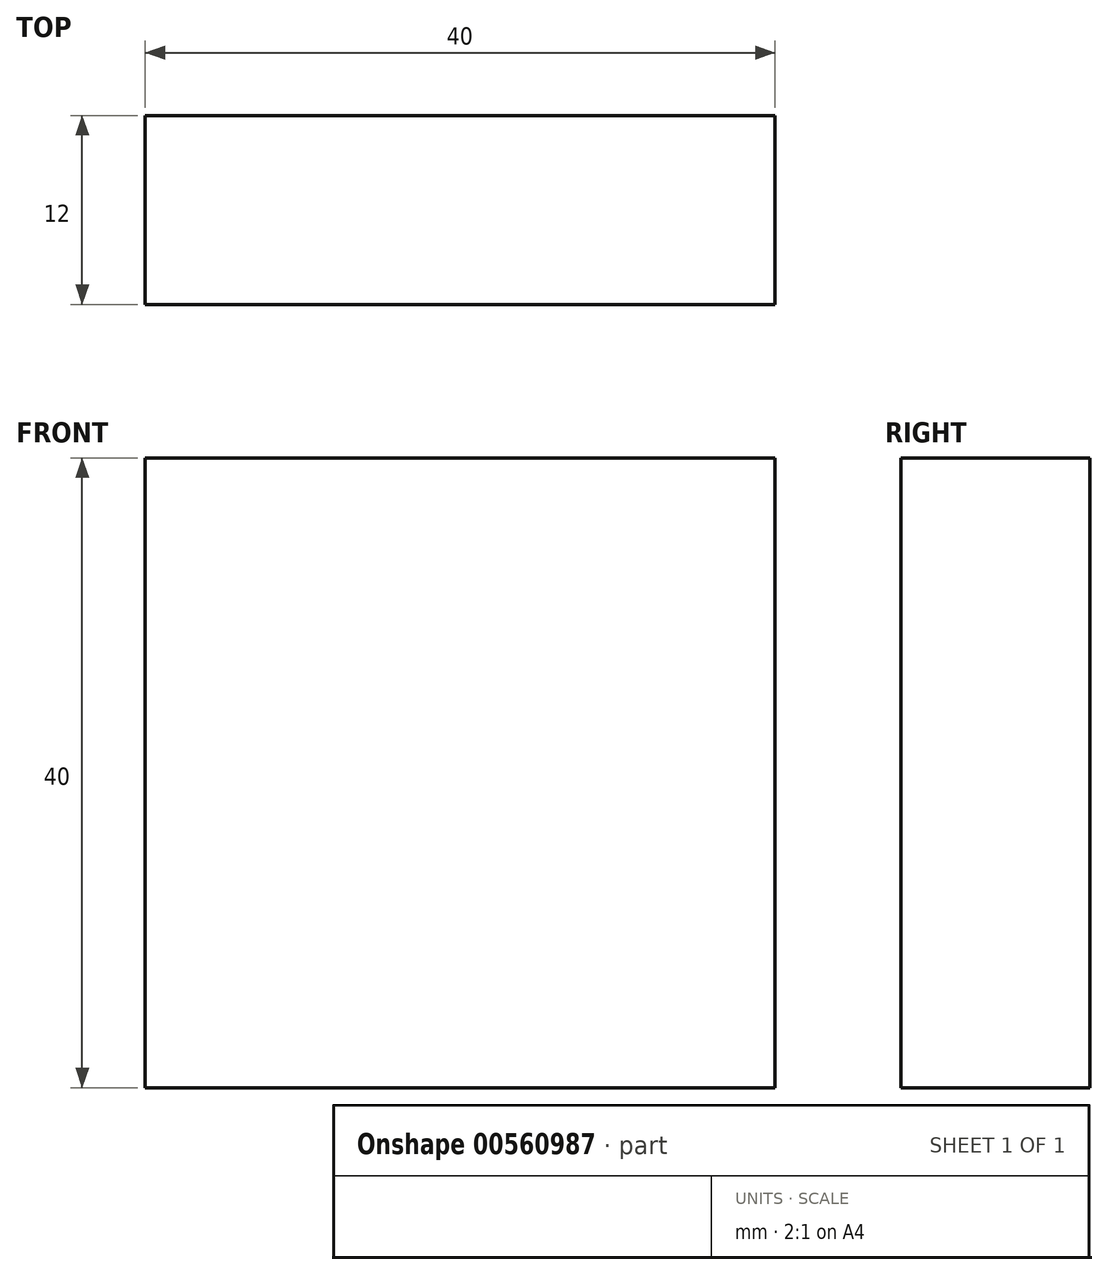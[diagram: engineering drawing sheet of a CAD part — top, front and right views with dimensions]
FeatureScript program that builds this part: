
annotation { "Feature Type Name" : "Feature", "Feature Type Description" : "" }
export const myFeature = defineFeature(function(context is Context, id is Id, definition is map)
    precondition{}
    {
        {
            var Q0;
            Q0=qCreatedBy(makeId("Front.planeOp"),FACE);
            var sketch = newSketch(context, id + "F0", { "sketchPlane" : qUnion([Q0])});
            skLineSegment(sketch, "E0.bottom", {"start": v(20, -20) * mm, "end": v(-20, -20) * mm});
            skLineSegment(sketch, "E0.top", {"start": v(20, 20) * mm, "end": v(-20, 20) * mm});
            skLineSegment(sketch, "E0.left", {"start": v(20, -20) * mm, "end": v(20, 20) * mm});
            skLineSegment(sketch, "E0.right", {"start": v(-20, -20) * mm, "end": v(-20, 20) * mm});
            skPoint(sketch, "E0.middle", {"position": v(0, 0) * mm});
            skSolve(sketch);
        }
        {
            var Q0;
            Q0=qSketchRegion(id+"F0",true);
            extrude(context, id + "F1", {"entities" : qUnion([Q0]), "endBound" : BoundingType.SYMMETRIC, "depth" : 12 * mm});
        }
    });
